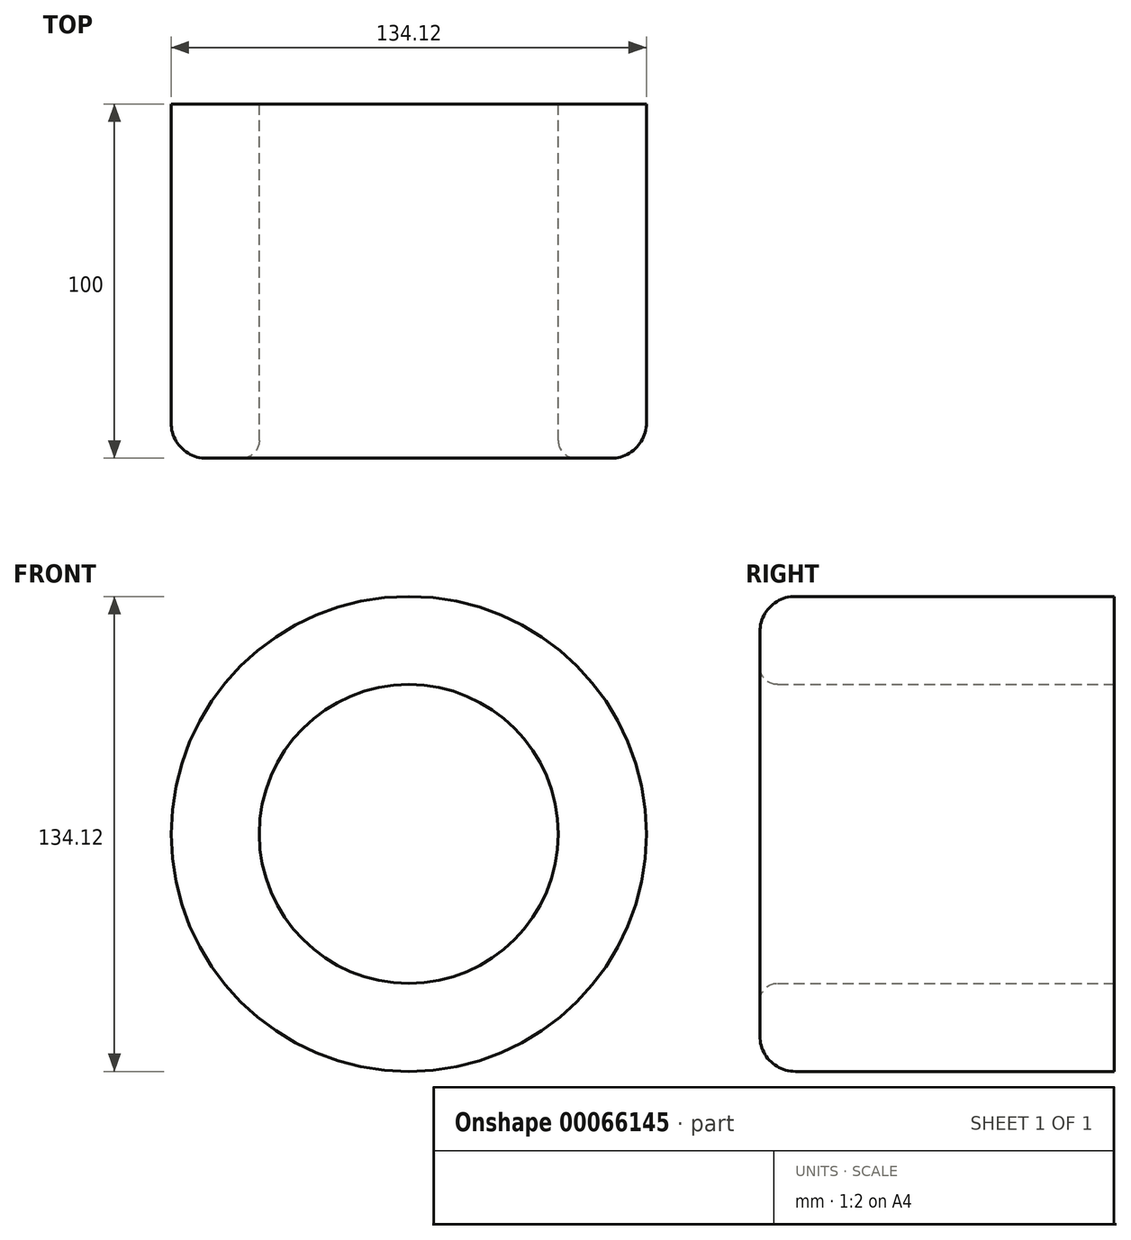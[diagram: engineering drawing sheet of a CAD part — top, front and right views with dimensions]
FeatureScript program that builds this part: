
annotation { "Feature Type Name" : "Feature", "Feature Type Description" : "" }
export const myFeature = defineFeature(function(context is Context, id is Id, definition is map)
    precondition{}
    {
        {
            var Q0;
            Q0=qCreatedBy(makeId("Front.planeOp"),FACE);
            var sketch = newSketch(context, id + "F0", { "sketchPlane" : qUnion([Q0])});
            skCircle(sketch, "E0", {"center": v(0, 0) * mm, "radius": 67.06 * mm});
            skCircle(sketch, "E1", {"center": v(0, 0) * mm, "radius": 42.18 * mm});
            skSolve(sketch);
        }
        {
            var Q0;
            Q0 = qSketchRegion(id + "F0", true);
            extrude(context, id + "F1", {"entities" : qUnion([Q0]), "depth" : 100 * mm});
        }
        {
            var Q0;
            Q0=makeQuery(id+"F1.opExtrude","CAP_EDGE",EDGE,{"disambiguationData":[OSD([sQuery(id+"F0.wireOp",EDGE,"E0")])],"isStart":false});
            fillet(context, id + "F2", {"entities" : qUnion([Q0]), "radius" : 10 * mm, "tangentPropagation" : true, "allowEdgeOverflow" : false});
        }
        {
            var Q0;
            Q0=makeQuery(id+"F1.opExtrude","CAP_EDGE",EDGE,{"disambiguationData":[OSD([sQuery(id+"F0.wireOp",EDGE,"E1")])],"isStart":false});
            fillet(context, id + "F3", {"entities" : qUnion([Q0]), "radius" : 5 * mm, "tangentPropagation" : true, "allowEdgeOverflow" : false});
        }
    });
